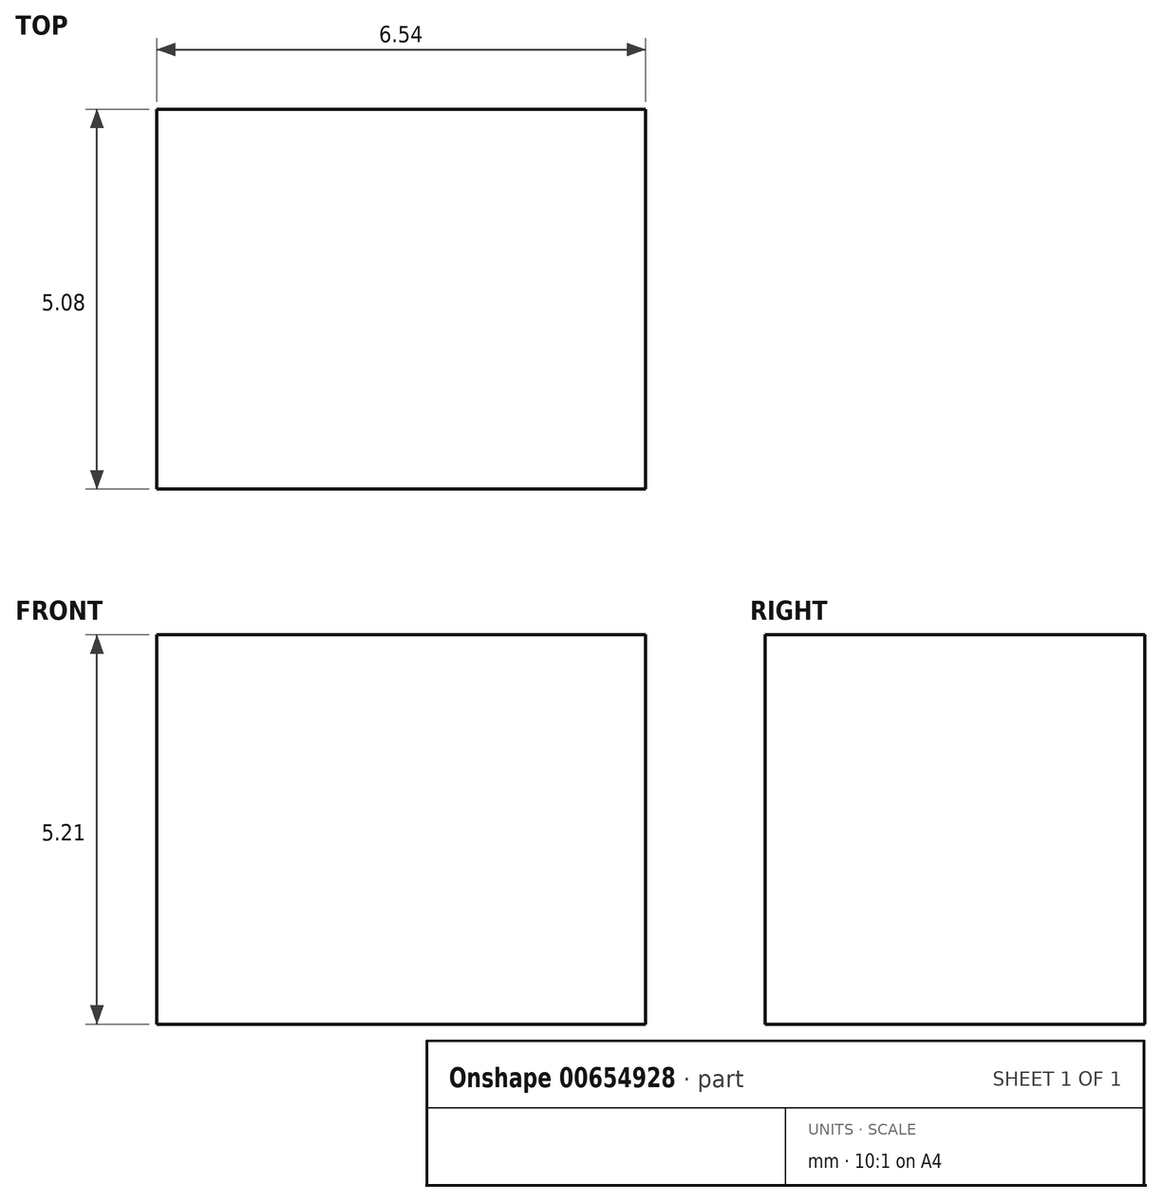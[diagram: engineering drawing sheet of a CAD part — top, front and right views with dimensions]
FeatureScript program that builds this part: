
annotation { "Feature Type Name" : "Feature", "Feature Type Description" : "" }
export const myFeature = defineFeature(function(context is Context, id is Id, definition is map)
    precondition{}
    {
        {
            var Q0;
            Q0=qCreatedBy(makeId("Front.planeOp"),FACE);
            var sketch = newSketch(context, id + "F0", { "sketchPlane" : qUnion([Q0])});
            skLineSegment(sketch, "E0", {"start": v(0, 0) * mm, "end": v(6.54, 0) * mm});
            skLineSegment(sketch, "E1", {"start": v(6.54, 0) * mm, "end": v(6.54, 5.2) * mm});
            skLineSegment(sketch, "E2", {"start": v(6.54, 5.2) * mm, "end": v(0, 5.2) * mm});
            skLineSegment(sketch, "E3", {"start": v(0, 5.2) * mm, "end": v(0, 0) * mm});
            skSolve(sketch);
        }
        {
            var Q0;
            Q0=makeQuery(id+"F0.imprint","IMPRINT",FACE,{"disambiguationData":[TD([[makeQuery(id+"F0.imprint","IMPRINT",EDGE,{"derivedFrom":sQuery(id+"F0.wireOp",EDGE,"E0")}),1.0]])]});
            extrude(context, id + "F1", {"entities" : qUnion([Q0]), "depth" : 5.08 * mm, "offsetDistance" : 25.4 * mm});
        }
    });
